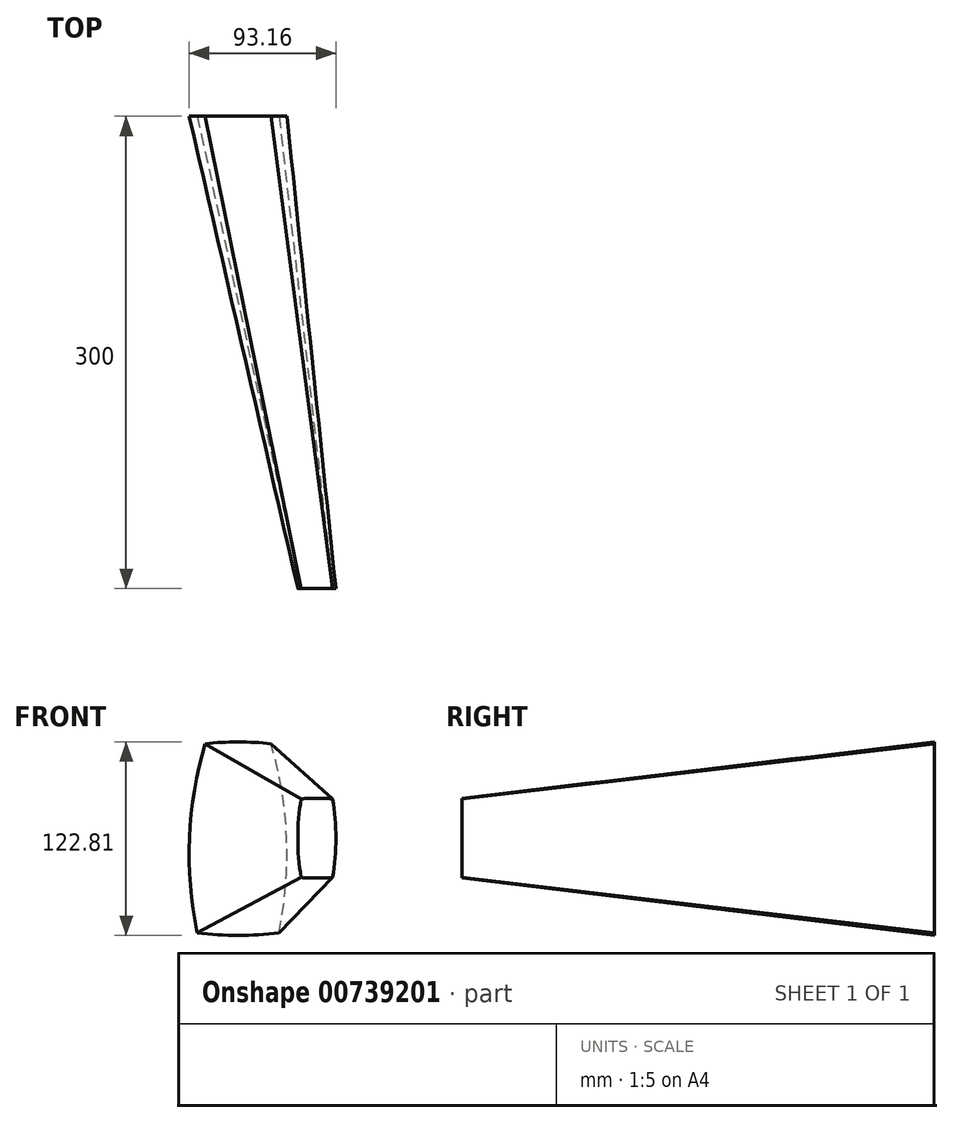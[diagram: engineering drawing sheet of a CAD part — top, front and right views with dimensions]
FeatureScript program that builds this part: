
annotation { "Feature Type Name" : "Feature", "Feature Type Description" : "" }
export const myFeature = defineFeature(function(context is Context, id is Id, definition is map)
    precondition{}
    {
        {
            var Q0;
            Q0=qCreatedBy(makeId("Front.planeOp"),FACE);
            var sketch = newSketch(context, id + "F0", { "sketchPlane" : qUnion([Q0])});
            skPoint(sketch, "E0", {"position": v(-21, 60) * mm});
            skPoint(sketch, "E1", {"position": v(21, 60) * mm});
            skPoint(sketch, "E2", {"position": v(26, -60) * mm});
            skPoint(sketch, "E3", {"position": v(-26, -60) * mm});
            skLineSegment(sketch, "E4", {"start": v(0, 67.9) * mm, "end": v(0, -71.1) * mm, "construction": true});
            skLineSegment(sketch, "E5", {"start": v(-70.4, 0) * mm, "end": v(69.68, 0) * mm, "construction": true});
            skArc(sketch, "E6", {"start": v(-21, 60) * mm, "mid": v(-30.81, 0.3) * mm, "end": v(-26, -60) * mm});
            skArc(sketch, "E7", {"start": v(-26, -60) * mm, "mid": v(0, -61.7) * mm, "end": v(26, -60) * mm});
            skArc(sketch, "E8", {"start": v(26, -60) * mm, "mid": v(30.81, 0.3) * mm, "end": v(21, 60) * mm});
            skArc(sketch, "E9", {"start": v(21, 60) * mm, "mid": v(0, 61.1) * mm, "end": v(-21, 60) * mm});
            skSolve(sketch);
        }
        {
            var Q0;
            Q0=qCreatedBy(makeId("Front.planeOp"),FACE);
            cPlane(context, id + "F1", {"entities" : qUnion([Q0]), "cplaneType" : CPlaneType.OFFSET, "offset" : 300 * mm, "width" : 150 * mm, "height" : 150 * mm});
        }
        {
            var Q0;
            Q0=qCreatedBy(id+"F1.planeOp",FACE);
            var sketch = newSketch(context, id + "F2", { "sketchPlane" : qUnion([Q0])});
            skPoint(sketch, "E10", {"position": v(40.04, 25) * mm});
            skPoint(sketch, "E11", {"position": v(60.04, 25) * mm});
            skPoint(sketch, "E12", {"position": v(60.04, -25) * mm});
            skPoint(sketch, "E13", {"position": v(40.04, -25) * mm});
            skLineSegment(sketch, "E14", {"start": v(0.04, 32.9) * mm, "end": v(0.04, -106.1) * mm, "construction": true});
            skLineSegment(sketch, "E15", {"start": v(-9.36, 0) * mm, "end": v(130.72, 0) * mm, "construction": true});
            skArc(sketch, "E16", {"start": v(40.04, 25) * mm, "mid": v(37.94, 0) * mm, "end": v(40.04, -25) * mm});
            skArc(sketch, "E17", {"start": v(40.04, -25) * mm, "mid": v(50.04, -25.33) * mm, "end": v(60.04, -25) * mm});
            skArc(sketch, "E18", {"start": v(60.04, -25) * mm, "mid": v(62.13, 0) * mm, "end": v(60.04, 25) * mm});
            skArc(sketch, "E19", {"start": v(60.04, 25) * mm, "mid": v(50.04, 25.33) * mm, "end": v(40.04, 25) * mm});
            skLineSegment(sketch, "E20", {"start": v(50.04, 101.73) * mm, "end": v(50.04, -165.05) * mm, "construction": true});
            skPoint(sketch, "E21", {"position": v(0, 0) * mm});
            skSolve(sketch);
        }
        {
            var Q0;
            Q0 = qSketchRegion(id + "F0", true);
            var Q1;
            Q1 = qSketchRegion(id + "F2", true);
            var Q2;
            Q2=sQuery(id+"F2.wireOp",VERTEX,"E10");
            var Q3;
            Q3=sQuery(id+"F0.wireOp",VERTEX,"E0");
            loft(context, id + "F3", {"sheetProfilesArray" : [{ "sheetProfileEntities" : qUnion([Q0]) }, { "sheetProfileEntities" : qUnion([Q1]) }], "matchConnections" : true, "connections" : [{ "connectionEntities" : qUnion([Q2, Q3]), "connectionEdgeQueries" : qUnion([]), "connectionEdgeParameters" : [] }]});
        }
    });
